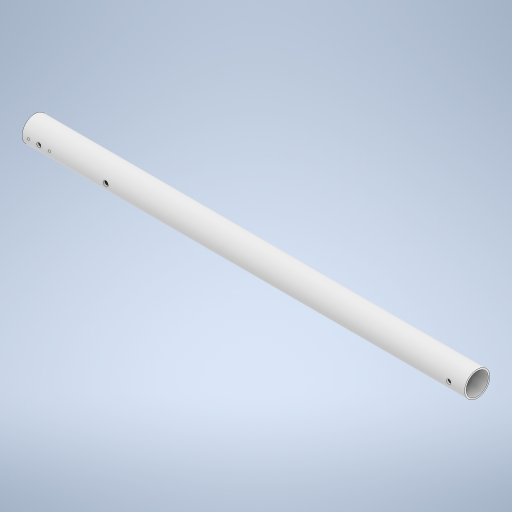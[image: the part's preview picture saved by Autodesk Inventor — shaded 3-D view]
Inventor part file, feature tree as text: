
AUTODESK INVENTOR PART (.ipt)
format: ipt  version: 2023 (Build 270158030, 158C)  size: 285,696 bytes
history: native  units: in
note: dims shown in document units (in); Inventor stores cm internally (conversion verified against a paired STEP export)
features: extrude x4, sketch x4
ambient origin geometry x8: Origin, YZ Plane, XZ Plane, XY Plane, X Axis, Y Axis, Z Axis, Center Point
bodies: Solid1 (feature_tree)
feature tree (8):
  extrude  "Extrusion1"  Depth=0.154in
  extrude  "Extrusion3"  Depth=0.4134in
  extrude  "Extrusion5"  TaperAngle=0.0deg  [1 undecoded]
  extrude  "Extrusion6"  Depth=0.1969in
  sketch  "Sketch1"  dims[d0=2.067in d1=0.154in]
  sketch  "Sketch3"  dims[d2=41.7323in d3=0.0in d8=0.4134in]
  sketch  "Sketch5"  dims[d9=1.5in d10=0.0in d11=0.0in]
  sketch  "Sketch6"  dims[d17=0.4724in d18=7.874in d19=0.0in d20=0.0in d21=0.3937in d22=1.5748in d23=0.0in d24=0.0in d25=1.9685in d26=0.1969in]
note: 1 required parameter value undecoded (feature->parameter linkage not recoverable at this tier; creation-order binding heuristic only, values carry confidence <= 0.55)
